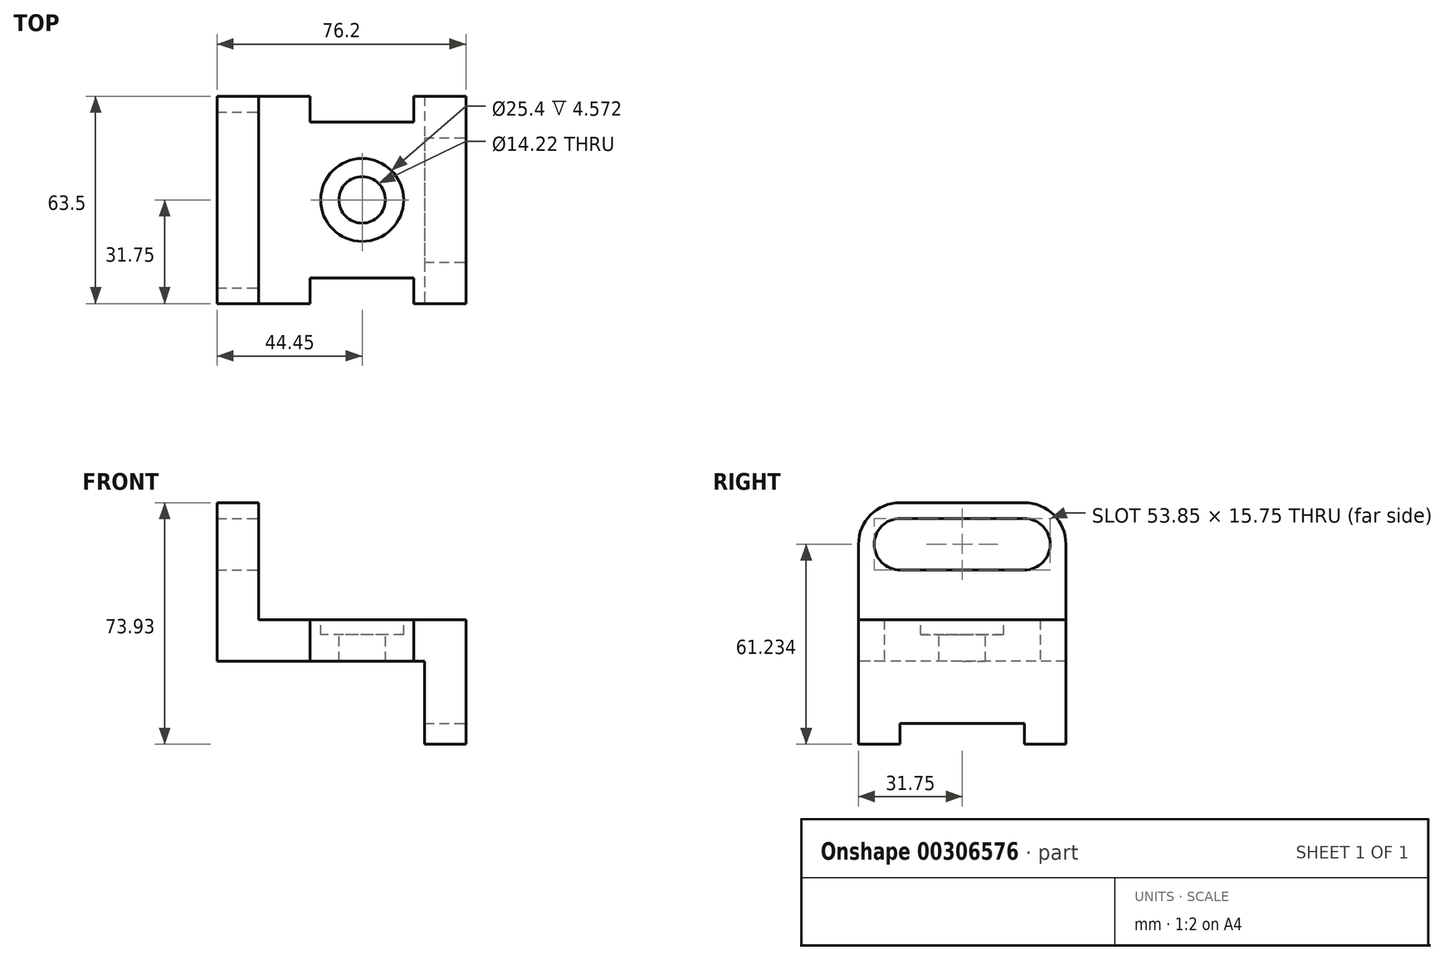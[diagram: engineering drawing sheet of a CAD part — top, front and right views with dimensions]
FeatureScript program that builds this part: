
annotation { "Feature Type Name" : "Feature", "Feature Type Description" : "" }
export const myFeature = defineFeature(function(context is Context, id is Id, definition is map)
    precondition{}
    {
        {
            var Q0;
            Q0=qCreatedBy(makeId("Front.planeOp"),FACE);
            var sketch = newSketch(context, id + "F0", { "sketchPlane" : qUnion([Q0])});
            skLineSegment(sketch, "E0", {"start": v(0, 0) * mm, "end": v(0, 38.1) * mm});
            skLineSegment(sketch, "E1", {"start": v(0, 38.1) * mm, "end": v(-16, 38.1) * mm});
            skLineSegment(sketch, "E2", {"start": v(-16, 38.1) * mm, "end": v(-16, 25.4) * mm});
            skLineSegment(sketch, "E3", {"start": v(-16, 25.4) * mm, "end": v(-12.7, 25.4) * mm});
            skLineSegment(sketch, "E4", {"start": v(-12.7, 25.4) * mm, "end": v(-12.7, 0) * mm});
            skLineSegment(sketch, "E5", {"start": v(-12.7, 0) * mm, "end": v(0, 0) * mm});
            skLineSegment(sketch, "E6", {"start": v(-16, 38.1) * mm, "end": v(-47.75, 38.1) * mm});
            skLineSegment(sketch, "E7", {"start": v(-63.5, 25.4) * mm, "end": v(-16, 25.4) * mm});
            skLineSegment(sketch, "E8", {"start": v(-63.5, 25.4) * mm, "end": v(-76.2, 25.4) * mm});
            skLineSegment(sketch, "E9", {"start": v(-76.2, 25.4) * mm, "end": v(-76.2, 73.93) * mm});
            skLineSegment(sketch, "E10", {"start": v(-76.2, 73.93) * mm, "end": v(-63.5, 73.93) * mm});
            skLineSegment(sketch, "E11", {"start": v(-47.75, 38.1) * mm, "end": v(-47.75, 25.4) * mm});
            skLineSegment(sketch, "E12", {"start": v(-63.5, 73.93) * mm, "end": v(-63.5, 38.1) * mm});
            skLineSegment(sketch, "E13", {"start": v(-63.5, 25.4) * mm, "end": v(-63.5, 38.1) * mm});
            skLineSegment(sketch, "E14", {"start": v(-63.5, 38.1) * mm, "end": v(-47.75, 38.1) * mm});
            skSolve(sketch);
        }
        {
            var Q0;
            Q0 = qSketchRegion(id + "F0", true);
            extrude(context, id + "F1", {"entities" : qUnion([Q0]), "oppositeDirection" : true, "depth" : 63.5 * mm});
        }
        {
            var Q0;
            {var subQ0=sQuery(id+"F0.wireOp",EDGE,"E2");Q0=makeQuery(id+"F0.imprint","IMPRINT",FACE,{"disambiguationData":[TD([[makeQuery(id+"F0.imprint","IMPRINT",EDGE,{"derivedFrom":subQ0}),-1.0]])]});}
            extrude(context, id + "F2", {"entities" : qUnion([Q0]), "operationType" : NewBodyOperationType.REMOVE, "oppositeDirection" : true, "depth" : 7.87 * mm});
        }
        {
            var Q0;
            {var subQ0=sQuery(id+"F0.wireOp",EDGE,"E2");Q0=makeQuery(id+"F0.imprint","IMPRINT",FACE,{"disambiguationData":[TD([[makeQuery(id+"F0.imprint","IMPRINT",EDGE,{"derivedFrom":subQ0}),-1.0]])]});}
            extrude(context, id + "F3", {"entities" : qUnion([Q0]), "operationType" : NewBodyOperationType.REMOVE, "oppositeDirection" : true, "depth" : 63.5 * mm, "hasSecondDirection" : true, "secondDirectionOppositeDirection" : true, "secondDirectionDepth" : 55.63 * mm});
        }
        {
            var Q0;
            Q0=makeQuery(id+"F1.opExtrude","SWEPT_FACE",FACE,{"disambiguationData":[OSD([sQuery(id+"F0.wireOp",EDGE,"E0")])]});
            var sketch = newSketch(context, id + "F4", { "sketchPlane" : qUnion([Q0])});
            skLineSegment(sketch, "E15", {"start": v(0, 38.1) * mm, "end": v(0, 0) * mm});
            skLineSegment(sketch, "E16", {"start": v(0, 0) * mm, "end": v(12.7, 0) * mm});
            skLineSegment(sketch, "E17", {"start": v(12.7, 0) * mm, "end": v(12.7, 6.35) * mm});
            skLineSegment(sketch, "E18", {"start": v(12.7, 6.35) * mm, "end": v(50.8, 6.35) * mm});
            skLineSegment(sketch, "E19", {"start": v(50.8, 6.35) * mm, "end": v(50.8, 0) * mm});
            skLineSegment(sketch, "E20", {"start": v(50.8, 0) * mm, "end": v(63.5, 0) * mm});
            skLineSegment(sketch, "E21", {"start": v(63.5, 0) * mm, "end": v(63.5, 38.1) * mm});
            skLineSegment(sketch, "E22", {"start": v(63.5, 38.1) * mm, "end": v(0, 38.1) * mm});
            skSolve(sketch);
        }
        {
            var Q0;
            {var subQ0=sQuery(id+"F4.wireOp",EDGE,"E17");Q0=makeQuery(id+"F4.imprint","IMPRINT",FACE,{"disambiguationData":[TD([[makeQuery(id+"F4.imprint","IMPRINT",EDGE,{"derivedFrom":subQ0}),-1.0]])]});}
            extrude(context, id + "F5", {"entities" : qUnion([Q0]), "operationType" : NewBodyOperationType.REMOVE, "oppositeDirection" : true, "depth" : 25.4 * mm});
        }
        {
            var Q0;
            Q0=makeQuery(id+"F1.opExtrude","SWEPT_FACE",FACE,{"disambiguationData":[OSD([sQuery(id+"F0.wireOp",EDGE,"E1"),sQuery(id+"F0.wireOp",EDGE,"E6"),sQuery(id+"F0.wireOp",EDGE,"E14")])]});
            var sketch = newSketch(context, id + "F6", { "sketchPlane" : qUnion([Q0])});
            skCircle(sketch, "E23", {"center": v(-31.75, 31.75) * mm, "radius": 12.7 * mm});
            skCircle(sketch, "E24", {"center": v(-31.75, 31.75) * mm, "radius": 7.11 * mm});
            skSolve(sketch);
        }
        {
            var Q0;
            Q0=makeQuery(id+"F6.imprint","IMPRINT",FACE,{"disambiguationData":[TD([[makeQuery(id+"F6.imprint","IMPRINT",EDGE,{"derivedFrom":sQuery(id+"F6.wireOp",EDGE,"E23")}),1.0]])]});
            extrude(context, id + "F7", {"entities" : qUnion([Q0]), "operationType" : NewBodyOperationType.REMOVE, "oppositeDirection" : true, "depth" : 4.57 * mm});
        }
        {
            var Q0;
            Q0=makeQuery(id+"F7.boolean.opBoolean","SPLIT",FACE,{"disambiguationData":[TD([makeQuery(id+"F7.opExtrude","SWEPT_FACE",FACE,{"disambiguationData":[OSD([sQuery(id+"F6.wireOp",EDGE,"E24")])]})])],"derivedFrom":makeQuery(id+"F1.opExtrude","SWEPT_FACE",FACE,{"disambiguationData":[OSD([sQuery(id+"F0.wireOp",EDGE,"E1"),sQuery(id+"F0.wireOp",EDGE,"E6"),sQuery(id+"F0.wireOp",EDGE,"E14")])]})});
            extrude(context, id + "F8", {"entities" : qUnion([Q0]), "operationType" : NewBodyOperationType.REMOVE, "oppositeDirection" : true, "depth" : 25.4 * mm});
        }
        {
            var Q0;
            Q0=makeQuery(id+"F1.opExtrude","SWEPT_FACE",FACE,{"disambiguationData":[OSD([sQuery(id+"F0.wireOp",EDGE,"E12")])]});
            var sketch = newSketch(context, id + "F9", { "sketchPlane" : qUnion([Q0])});
            skArc(sketch, "E25", {"start": v(12.7, 69.1) * mm, "mid": v(4.83, 61.23) * mm, "end": v(12.7, 53.36) * mm});
            skLineSegment(sketch, "E26", {"start": v(12.7, 69.1) * mm, "end": v(50.8, 69.1) * mm});
            skArc(sketch, "E27", {"start": v(12.7, 73.93) * mm, "mid": v(3.72, 70.21) * mm, "end": v(0, 61.23) * mm});
            skPoint(sketch, "E27.endSnap0", {"position": v(4.83, 61.23) * mm});
            skArc(sketch, "E28", {"start": v(63.5, 61.23) * mm, "mid": v(59.78, 70.21) * mm, "end": v(50.8, 73.93) * mm});
            skArc(sketch, "E29", {"start": v(50.8, 53.36) * mm, "mid": v(58.67, 61.23) * mm, "end": v(50.8, 69.1) * mm});
            skLineSegment(sketch, "E30", {"start": v(12.7, 53.36) * mm, "end": v(50.8, 53.36) * mm});
            skSolve(sketch);
        }
        {
            var Q0;
            {var subQ0=sQuery(id+"F9.wireOp",EDGE,"E28");Q0=makeQuery(id+"F9.imprint","IMPRINT",FACE,{"disambiguationData":[TD([[makeQuery(id+"F9.imprint","IMPRINT",EDGE,{"derivedFrom":subQ0}),-1.0]])]});}
            var Q1;
            {var subQ0=sQuery(id+"F9.wireOp",EDGE,"E27");Q1=makeQuery(id+"F9.imprint","IMPRINT",FACE,{"disambiguationData":[TD([[makeQuery(id+"F9.imprint","IMPRINT",EDGE,{"derivedFrom":subQ0}),-1.0]])]});}
            extrude(context, id + "F10", {"entities" : qUnion([Q0, Q1]), "operationType" : NewBodyOperationType.REMOVE, "oppositeDirection" : true, "depth" : 25.4 * mm});
        }
        {
            var Q0;
            Q0=makeQuery(id+"F9.imprint","IMPRINT",FACE,{"disambiguationData":[TD([[makeQuery(id+"F9.imprint","IMPRINT",EDGE,{"derivedFrom":sQuery(id+"F9.wireOp",EDGE,"E25")}),1.0]])]});
            extrude(context, id + "F11", {"entities" : qUnion([Q0]), "operationType" : NewBodyOperationType.REMOVE, "oppositeDirection" : true, "depth" : 25.4 * mm});
        }
    });
